# Revit family: Sanitary_Taps-Mixers_AXOR_36723USA-AXOR-ShowerSolutions-Thermostat_юю
name_source: partatom
category: Plumbing Fixtures
revit_build: Autodesk Revit 2018 (Build: 20170223_1515(x64)
units: mm (PartAtom-declared; Revit-internal decimal feet)

## family parameters
Always vertical = No
Cut with Voids When Loaded = No
OmniClass Number = 23.27.31.29.15
OmniClass Title = Thermostatically Controlled Mixing Valves
Part Type = Normal
Room Calculation Point = No
Round Connector Dimension = Use Diameter
Shared = No
Work Plane-Based = Yes

## types (5) — shared parameters
BIMobject category = Taps & Mixers
Default Elevation = 1219.2 mm  [stored 4 ft]
Description = AXOR ShowerSolutions Thermostat for concealed installation round for 2 functions
Design country = Germany
EAN code = 4011097797298
Edition number = 1
GTIN code = https://4011097797298
IFC Classification = Valve
Installation instructions = https://www.axor-design.com
Manufacturer = AXOR
Manufacturer country = Germany
Manufacturer name = AXOR
Material 1 = AXOR - Plastic - Dark Gray
Model = 36723USA
OmniClass Code = 23-27 31 29 15
OmniClass Description = Thermostatically Controlled Mixing Valves
Product Guid = 619b06ae-ccb4-4d18-86ac-941f5ad5dea9
Product SKU = 36723USA
Product data url = https://bimobject.com
Product family = AXOR ShowerSolutions
Product group = Shower thermostat
Product name = 36723USA AXOR ShowerSolutions Thermostat for concealed installation round for 2 functions
Product url = https://www.axor-design.com
QR code = https://bimobject.com
URL = https://www.axor-design.com
Weight Net (Kg) = 2,6

## per-type parameters (varying)
| type | Material 2 |
| 001 Chrome | AXOR - Metal - 001 Chrome |
| 671 Matt Black | AXOR - Metal - 671 Matt Black |
| 251 Brushed Gold Optic | AXOR - Metal - 251 Brushed Gold Optic |
| 341 Brushed Black Chrome | AXOR - Metal - 341 Brushed Black Chrome |
| 821 Brushed Nickel | AXOR - Metal - 821 Brushed Nickel |

note: [stored X ft] marks values corroborated as IEEE doubles in the binary element streams (Revit-internal decimal feet)

## geometry (parser evidence)
native form markers: Sweep x2
no freeform markers — native parametric forms only
